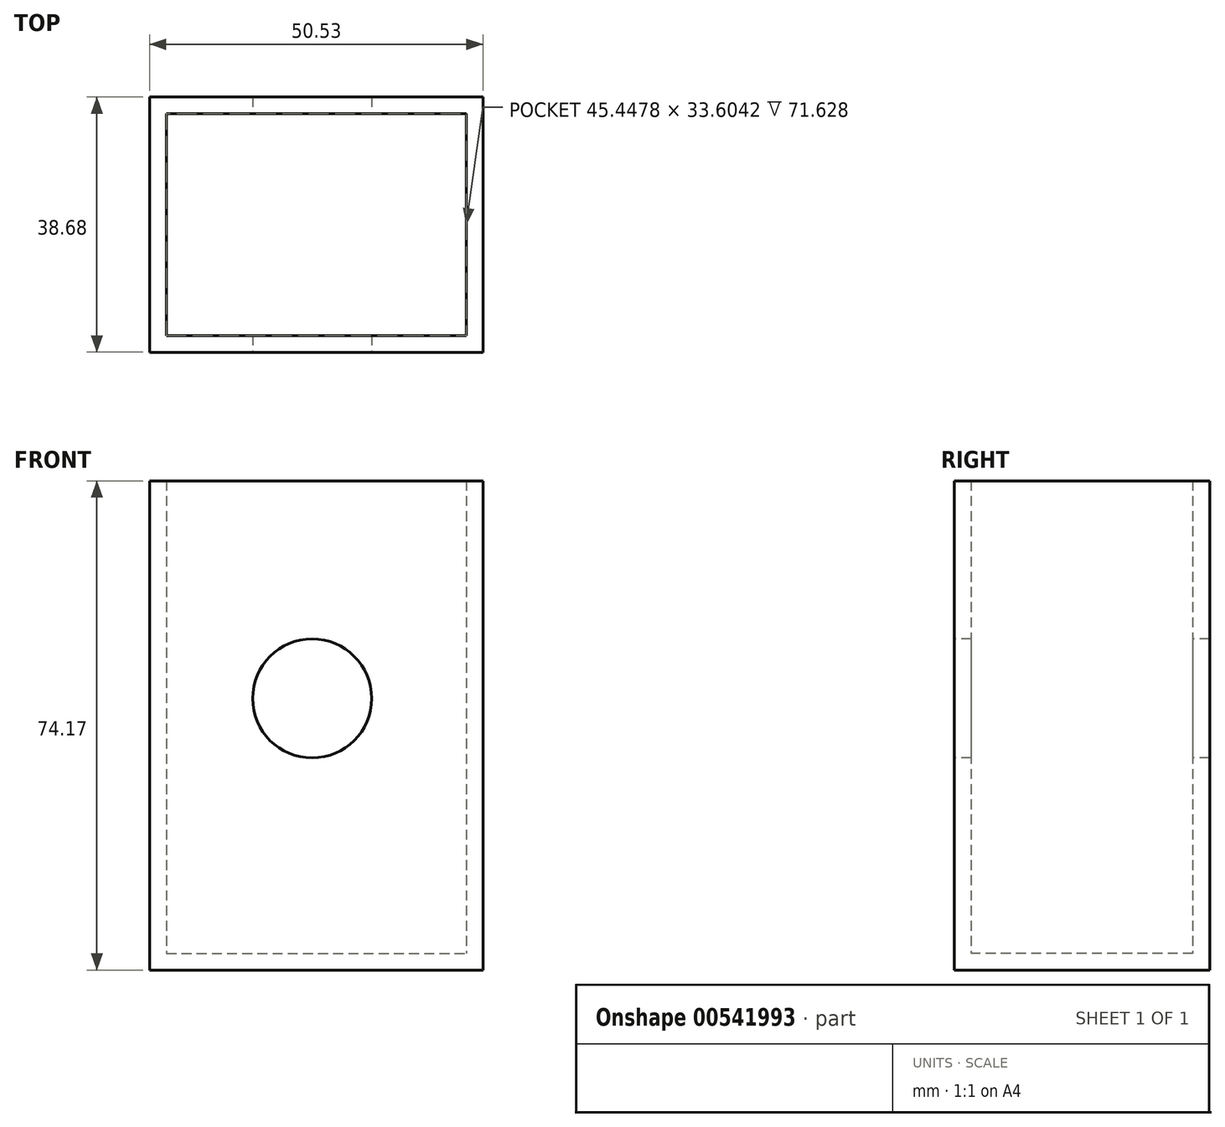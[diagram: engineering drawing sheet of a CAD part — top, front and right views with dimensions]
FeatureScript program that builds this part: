
annotation { "Feature Type Name" : "Feature", "Feature Type Description" : "" }
export const myFeature = defineFeature(function(context is Context, id is Id, definition is map)
    precondition{}
    {
        {
            var Q0;
            Q0=qCreatedBy(makeId("Top.planeOp"),FACE);
            var sketch = newSketch(context, id + "F0", { "sketchPlane" : qUnion([Q0])});
            skLineSegment(sketch, "E0.bottom", {"start": v(0, 0) * mm, "end": v(50.53, 0) * mm});
            skLineSegment(sketch, "E0.top", {"start": v(0, -38.68) * mm, "end": v(50.53, -38.68) * mm});
            skLineSegment(sketch, "E0.left", {"start": v(0, 0) * mm, "end": v(0, -38.68) * mm});
            skLineSegment(sketch, "E0.right", {"start": v(50.53, 0) * mm, "end": v(50.53, -38.68) * mm});
            skSolve(sketch);
        }
        {
            var Q0;
            Q0=makeQuery(id+"F0.imprint","IMPRINT",FACE,{"disambiguationData":[TD([[makeQuery(id+"F0.imprint","IMPRINT",EDGE,{"derivedFrom":sQuery(id+"F0.wireOp",EDGE,"E0.bottom")}),-1.0]])]});
            extrude(context, id + "F1", {"entities" : qUnion([Q0]), "depth" : 74.17 * mm, "offsetDistance" : 25.4 * mm});
        }
        {
            var Q0;
            Q0=makeQuery(id+"F1.opExtrude","CAP_FACE",FACE,{"disambiguationData":[OSD([sQuery(id+"F0.wireOp",EDGE,"E0.bottom"),sQuery(id+"F0.wireOp",EDGE,"E0.top"),sQuery(id+"F0.wireOp",EDGE,"E0.left"),sQuery(id+"F0.wireOp",EDGE,"E0.right")])],"isStart":false});
            shell(context, id + "F2", {"entities" : qUnion([Q0]), "thickness" : 2.54 * mm});
        }
        {
            var Q0;
            Q0=makeQuery(id+"F1.opExtrude","SWEPT_FACE",FACE,{"disambiguationData":[OSD([sQuery(id+"F0.wireOp",EDGE,"E0.top")])]});
            var sketch = newSketch(context, id + "F3", { "sketchPlane" : qUnion([Q0])});
            skCircle(sketch, "E1", {"center": v(24.64, 41.18) * mm, "radius": 9.02 * mm});
            skSolve(sketch);
        }
        {
            var Q0;
            Q0 = qSketchRegion(id + "F3", true);
            extrude(context, id + "F4", {"entities" : qUnion([Q0]), "operationType" : NewBodyOperationType.REMOVE, "oppositeDirection" : true, "depth" : 71.88 * mm, "offsetDistance" : 25.4 * mm});
        }
    });
